# Revit family: ALMA-Amos_Circle_Rustic_Concrete_Basin
name_source: partatom
category: Plumbing Equipment
units: mm (PartAtom-declared; Revit-internal decimal feet)

## family parameters
Classification = None
Cut with Voids When Loaded = No
Host = Face
Maintain Annotation Orientation = No
Part Type = Normal
Room Calculation Point = No
Round Connector Dimension = Use Diameter
Shared = No

## types (5) — shared parameters
Default Elevation = 1219 mm
Height = 125 mm
MainBody_Material = BM_STAINLESS STEEL
Width = 360 mm  [stored 1.1811 ft]

## per-type parameters (varying)
| type | Basin_Material | PopUp_Material |
| AMOS SEA SALT WHITE (CBAMOWH5) | BM_SEA SALT WHITE_CONC_TEXTURED | BM_SEA SALT WHITE_CONC |
| AMOS CHAMPAGNE PINK (CBAMOPN3) | BM_CHAMPAGNE PINK_CONC_TEXTURED | BM_CHAMPAGNE PINK_CONC |
| AMOS FOREST GREEN (CBAMOGR2) | BM_FOREST GREEN_CONC_TEXTURED | BM_FOREST GREEN_CONC |
| AMOS METEOR GREY (CBAMOGR4) | BM_METEOR GREY_CONC_TEXTURED | BM_METEOR GREY_CONC |
| AMOS TERRACOTTA (CBAMOTE1) | BM_TERRACOTTA_CONC_TEXTURED | BM_TERRACOTTA_CONC |

note: [stored X ft] marks values corroborated as IEEE doubles in the binary element streams (Revit-internal decimal feet)

## geometry (parser evidence)
native form markers: Sweep x1
no freeform markers — native parametric forms only
